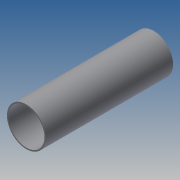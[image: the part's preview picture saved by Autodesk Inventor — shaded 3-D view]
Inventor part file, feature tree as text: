
AUTODESK INVENTOR PART (.ipt)
format: ipt  version: 2014 SP1 (Build 180222100, 222)  size: 77,824 bytes
history: native  units: in
note: dims shown in document units (in); Inventor stores cm internally (conversion verified against a paired STEP export)
features: extrude x1, sketch x1
ambient origin geometry x8: Origin, YZ Plane, XZ Plane, XY Plane, X Axis, Y Axis, Z Axis, Center Point
bodies: Solid1 (feature_tree)
feature tree (2):
  extrude  "Extrusion1"  Depth=19.685in
  sketch  "Sketch1"  dims[d1=0.2in d2=6.0in d3=19.685in d4=0.0in]
